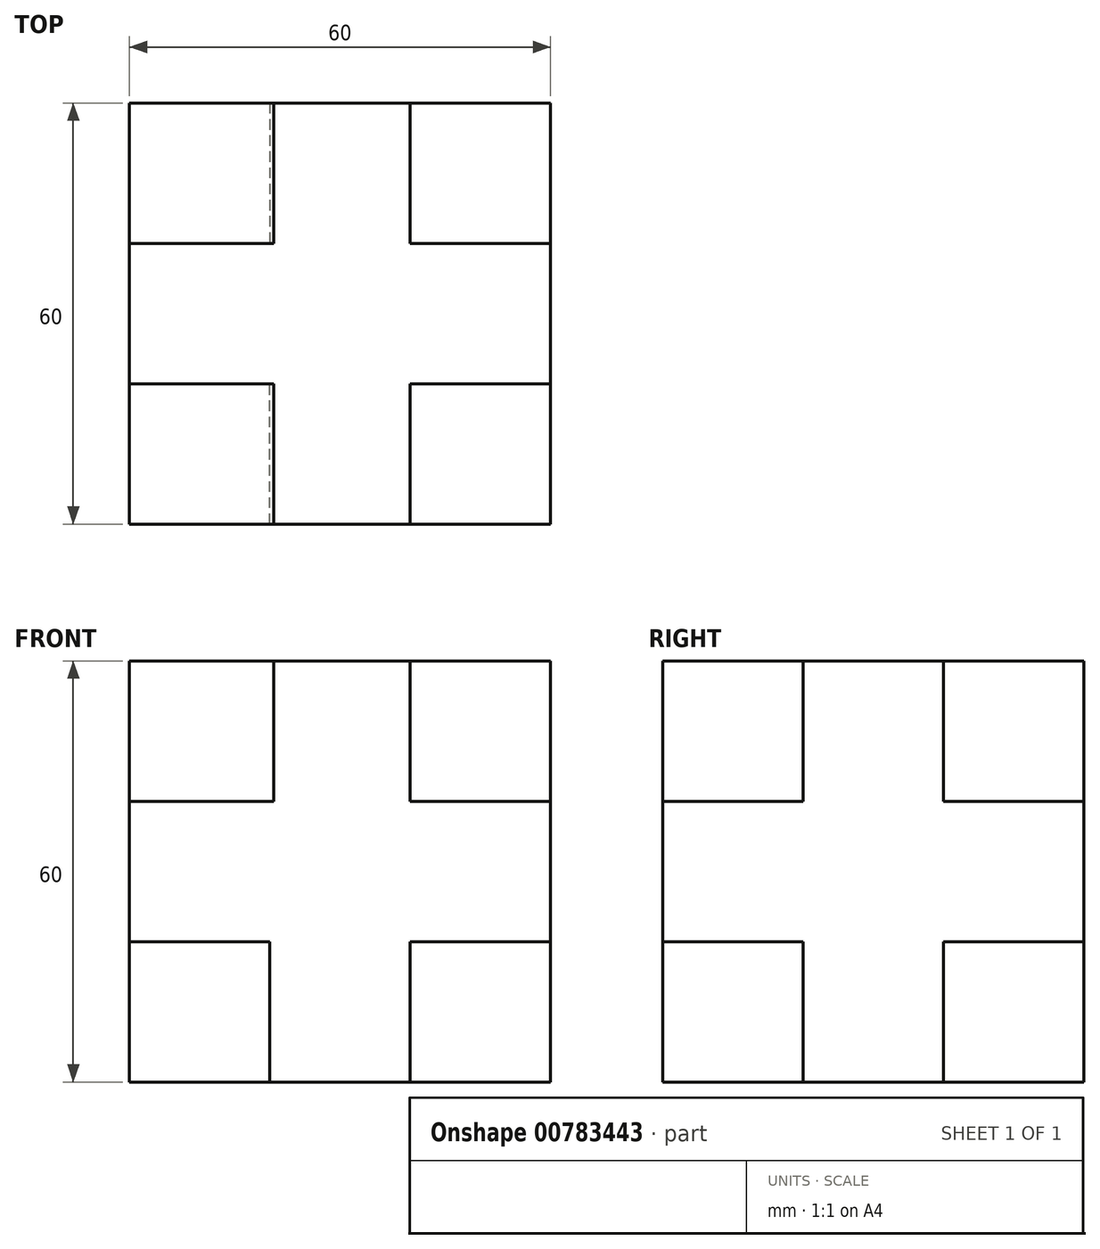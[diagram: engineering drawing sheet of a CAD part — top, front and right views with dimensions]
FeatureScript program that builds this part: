
annotation { "Feature Type Name" : "Feature", "Feature Type Description" : "" }
export const myFeature = defineFeature(function(context is Context, id is Id, definition is map)
    precondition{}
    {
        {
            var Q0;
            Q0=qCreatedBy(makeId("Top.planeOp"),FACE);
            var sketch = newSketch(context, id + "F0", { "sketchPlane" : qUnion([Q0])});
            skLineSegment(sketch, "E0.bottom", {"start": v(30, 30) * mm, "end": v(-30, 30) * mm});
            skLineSegment(sketch, "E0.top", {"start": v(30, -30) * mm, "end": v(-30, -30) * mm});
            skLineSegment(sketch, "E0.left", {"start": v(30, 30) * mm, "end": v(30, -30) * mm});
            skLineSegment(sketch, "E0.right", {"start": v(-30, 30) * mm, "end": v(-30, -30) * mm});
            skPoint(sketch, "E0.middle", {"position": v(0, 0) * mm});
            skSolve(sketch);
        }
        {
            var Q0;
            Q0 = qSketchRegion(id + "F0", true);
            extrude(context, id + "F1", {"entities" : qUnion([Q0]), "depth" : 60 * mm, "offsetDistance" : 25 * mm});
        }
        {
            var Q0;
            Q0=makeQuery(id+"F1.opExtrude","CAP_FACE",FACE,{"disambiguationData":[OSD([sQuery(id+"F0.wireOp",EDGE,"E0.bottom"),sQuery(id+"F0.wireOp",EDGE,"E0.top"),sQuery(id+"F0.wireOp",EDGE,"E0.left"),sQuery(id+"F0.wireOp",EDGE,"E0.right")])],"isStart":false});
            var sketch = newSketch(context, id + "F2", { "sketchPlane" : qUnion([Q0])});
            skLineSegment(sketch, "E1.bottom", {"start": v(-30, 30) * mm, "end": v(-9.45, 30) * mm});
            skLineSegment(sketch, "E1.top", {"start": v(-30, 10) * mm, "end": v(-9.45, 10) * mm});
            skLineSegment(sketch, "E1.left", {"start": v(-30, 30) * mm, "end": v(-30, 10) * mm});
            skLineSegment(sketch, "E1.right", {"start": v(-9.45, 30) * mm, "end": v(-9.45, 10) * mm});
            skLineSegment(sketch, "E2.bottom", {"start": v(-30, -30) * mm, "end": v(-9.45, -30) * mm});
            skLineSegment(sketch, "E2.top", {"start": v(-30, -10) * mm, "end": v(-9.45, -10) * mm});
            skLineSegment(sketch, "E2.left", {"start": v(-30, -30) * mm, "end": v(-30, -10) * mm});
            skLineSegment(sketch, "E2.right", {"start": v(-9.45, -30) * mm, "end": v(-9.45, -10) * mm});
            skLineSegment(sketch, "E3.bottom", {"start": v(30, -30) * mm, "end": v(10, -30) * mm});
            skLineSegment(sketch, "E3.top", {"start": v(30, -10) * mm, "end": v(10, -10) * mm});
            skLineSegment(sketch, "E3.left", {"start": v(30, -30) * mm, "end": v(30, -10) * mm});
            skLineSegment(sketch, "E3.right", {"start": v(10, -30) * mm, "end": v(10, -10) * mm});
            skLineSegment(sketch, "E4.bottom", {"start": v(30, 30) * mm, "end": v(10, 30) * mm});
            skLineSegment(sketch, "E4.top", {"start": v(30, 10) * mm, "end": v(10, 10) * mm});
            skLineSegment(sketch, "E4.left", {"start": v(30, 30) * mm, "end": v(30, 10) * mm});
            skLineSegment(sketch, "E4.right", {"start": v(10, 30) * mm, "end": v(10, 10) * mm});
            skSolve(sketch);
        }
        {
            var Q0;
            Q0=makeQuery(id+"F2.imprint","IMPRINT",FACE,{"disambiguationData":[TD([[makeQuery(id+"F2.imprint","IMPRINT",EDGE,{"derivedFrom":sQuery(id+"F2.wireOp",EDGE,"E1.bottom")}),1.0]])]});
            var Q1;
            Q1=makeQuery(id+"F2.imprint","IMPRINT",FACE,{"disambiguationData":[TD([[makeQuery(id+"F2.imprint","IMPRINT",EDGE,{"derivedFrom":sQuery(id+"F2.wireOp",EDGE,"E4.bottom")}),1.0]])]});
            var Q2;
            Q2=makeQuery(id+"F2.imprint","IMPRINT",FACE,{"disambiguationData":[TD([[makeQuery(id+"F2.imprint","IMPRINT",EDGE,{"derivedFrom":sQuery(id+"F2.wireOp",EDGE,"E3.bottom")}),-1.0]])]});
            var Q3;
            Q3=makeQuery(id+"F2.imprint","IMPRINT",FACE,{"disambiguationData":[TD([[makeQuery(id+"F2.imprint","IMPRINT",EDGE,{"derivedFrom":sQuery(id+"F2.wireOp",EDGE,"E2.bottom")}),-1.0]])]});
            extrude(context, id + "F3", {"entities" : qUnion([Q0, Q1, Q2, Q3]), "operationType" : NewBodyOperationType.REMOVE, "oppositeDirection" : true, "depth" : 20 * mm, "offsetDistance" : 25 * mm});
        }
        {
            var Q0;
            Q0=makeQuery(id+"F1.opExtrude","CAP_FACE",FACE,{"disambiguationData":[OSD([sQuery(id+"F0.wireOp",EDGE,"E0.bottom"),sQuery(id+"F0.wireOp",EDGE,"E0.top"),sQuery(id+"F0.wireOp",EDGE,"E0.left"),sQuery(id+"F0.wireOp",EDGE,"E0.right")])],"isStart":true});
            var sketch = newSketch(context, id + "F4", { "sketchPlane" : qUnion([Q0])});
            skLineSegment(sketch, "E5.bottom", {"start": v(30, -30) * mm, "end": v(10, -30) * mm});
            skLineSegment(sketch, "E5.top", {"start": v(30, -10) * mm, "end": v(10, -10) * mm});
            skLineSegment(sketch, "E5.left", {"start": v(30, -30) * mm, "end": v(30, -10) * mm});
            skLineSegment(sketch, "E5.right", {"start": v(10, -30) * mm, "end": v(10, -10) * mm});
            skLineSegment(sketch, "E6.bottom", {"start": v(-30, -30) * mm, "end": v(-10, -30) * mm});
            skLineSegment(sketch, "E6.top", {"start": v(-30, -10) * mm, "end": v(-10, -10) * mm});
            skLineSegment(sketch, "E6.left", {"start": v(-30, -30) * mm, "end": v(-30, -10) * mm});
            skLineSegment(sketch, "E6.right", {"start": v(-10, -30) * mm, "end": v(-10, -10) * mm});
            skLineSegment(sketch, "E7.bottom", {"start": v(-30, 30) * mm, "end": v(-10, 30) * mm});
            skLineSegment(sketch, "E7.top", {"start": v(-30, 10) * mm, "end": v(-10, 10) * mm});
            skLineSegment(sketch, "E7.left", {"start": v(-30, 30) * mm, "end": v(-30, 10) * mm});
            skLineSegment(sketch, "E7.right", {"start": v(-10, 30) * mm, "end": v(-10, 10) * mm});
            skLineSegment(sketch, "E8.bottom", {"start": v(30, 30) * mm, "end": v(10, 30) * mm});
            skLineSegment(sketch, "E8.top", {"start": v(30, 10) * mm, "end": v(10, 10) * mm});
            skLineSegment(sketch, "E8.left", {"start": v(30, 30) * mm, "end": v(30, 10) * mm});
            skLineSegment(sketch, "E8.right", {"start": v(10, 30) * mm, "end": v(10, 10) * mm});
            skSolve(sketch);
        }
        {
            var Q0;
            Q0=makeQuery(id+"F4.imprint","IMPRINT",FACE,{"disambiguationData":[TD([[makeQuery(id+"F4.imprint","IMPRINT",EDGE,{"derivedFrom":sQuery(id+"F4.wireOp",EDGE,"E5.bottom")}),-1.0]])]});
            var Q1;
            Q1=makeQuery(id+"F4.imprint","IMPRINT",FACE,{"disambiguationData":[TD([[makeQuery(id+"F4.imprint","IMPRINT",EDGE,{"derivedFrom":sQuery(id+"F4.wireOp",EDGE,"E6.bottom")}),-1.0]])]});
            var Q2;
            Q2=makeQuery(id+"F4.imprint","IMPRINT",FACE,{"disambiguationData":[TD([[makeQuery(id+"F4.imprint","IMPRINT",EDGE,{"derivedFrom":sQuery(id+"F4.wireOp",EDGE,"E7.bottom")}),1.0]])]});
            var Q3;
            Q3=makeQuery(id+"F4.imprint","IMPRINT",FACE,{"disambiguationData":[TD([[makeQuery(id+"F4.imprint","IMPRINT",EDGE,{"derivedFrom":sQuery(id+"F4.wireOp",EDGE,"E8.bottom")}),1.0]])]});
            extrude(context, id + "F5", {"entities" : qUnion([Q0, Q1, Q2, Q3]), "operationType" : NewBodyOperationType.REMOVE, "oppositeDirection" : true, "depth" : 20 * mm, "offsetDistance" : 25 * mm});
        }
    });
